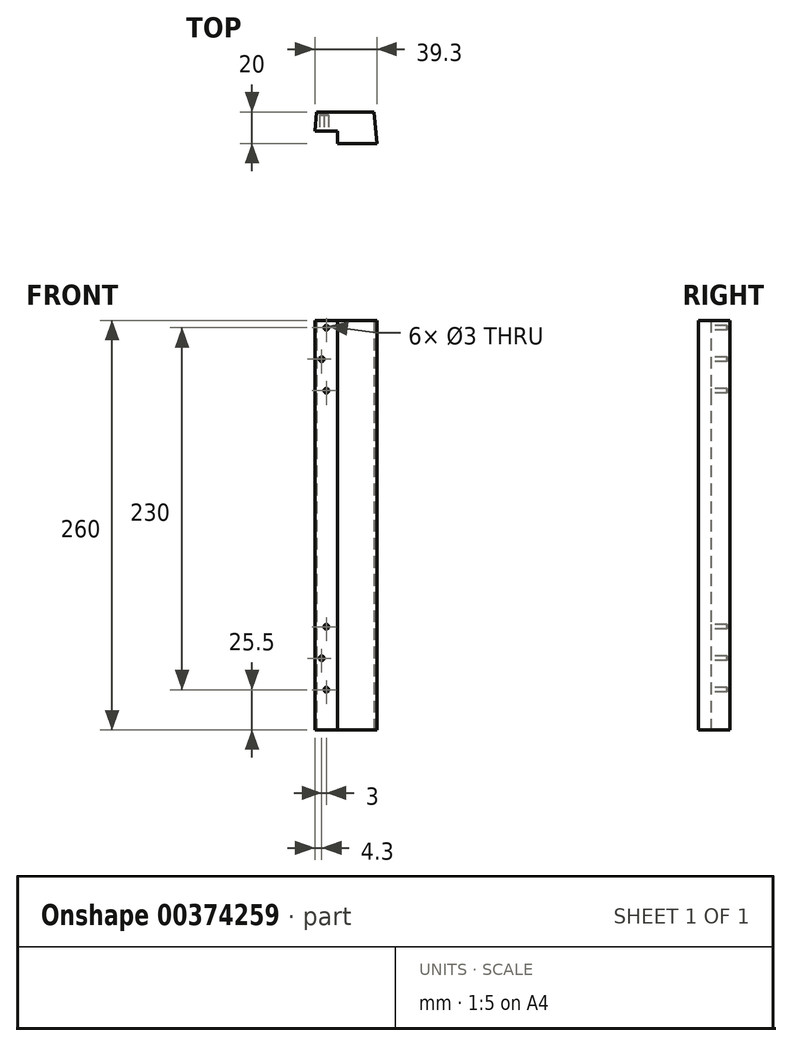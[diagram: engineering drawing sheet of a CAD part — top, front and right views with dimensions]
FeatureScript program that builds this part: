
annotation { "Feature Type Name" : "Feature", "Feature Type Description" : "" }
export const myFeature = defineFeature(function(context is Context, id is Id, definition is map)
    precondition{}
    {
        {
            var Q0;
            Q0=qCreatedBy(makeId("Top.planeOp"),FACE);
            var sketch = newSketch(context, id + "F0", { "sketchPlane" : qUnion([Q0])});
            skLineSegment(sketch, "E0", {"start": v(0.7, 8) * mm, "end": v(1.75, 20) * mm});
            skLineSegment(sketch, "E1", {"start": v(1.75, 20) * mm, "end": v(38.25, 20) * mm});
            skLineSegment(sketch, "E2", {"start": v(38.25, 20) * mm, "end": v(40, 0) * mm});
            skLineSegment(sketch, "E3", {"start": v(40, 0) * mm, "end": v(15, 0) * mm});
            skLineSegment(sketch, "E4", {"start": v(0.7, 8) * mm, "end": v(15, 8) * mm});
            skLineSegment(sketch, "E5", {"start": v(15, 8) * mm, "end": v(15, 0) * mm});
            skSolve(sketch);
        }
        {
            var Q0;
            Q0=makeQuery(id+"F0.imprint","IMPRINT",FACE,{"disambiguationData":[TD([[makeQuery(id+"F0.imprint","IMPRINT",EDGE,{"derivedFrom":sQuery(id+"F0.wireOp",EDGE,"E0")}),-1.0]])]});
            extrude(context, id + "F1", {"entities" : qUnion([Q0]), "depth" : 260 * mm});
        }
        {
            var Q0;
            Q0=makeQuery(id+"F1.opExtrude","SWEPT_FACE",FACE,{"disambiguationData":[OSD([sQuery(id+"F0.wireOp",EDGE,"E3")])]});
            var sketch = newSketch(context, id + "F2", { "sketchPlane" : qUnion([Q0])});
            skPoint(sketch, "E6", {"position": v(8, 255.5) * mm});
            skPoint(sketch, "E7", {"position": v(8, 215.5) * mm});
            skPoint(sketch, "E8", {"position": v(8, 65.5) * mm});
            skPoint(sketch, "E9", {"position": v(8, 25.5) * mm});
            skPoint(sketch, "E10", {"position": v(5, 45.5) * mm});
            skPoint(sketch, "E11", {"position": v(5, 235.5) * mm});
            skSolve(sketch);
        }
        {
            var Q0;
            Q0=sQuery(id+"F2.wireOp",VERTEX,"E6");
            var Q1;
            Q1=sQuery(id+"F2.wireOp",VERTEX,"E11");
            var Q2;
            Q2=sQuery(id+"F2.wireOp",VERTEX,"E7");
            var Q3;
            Q3=sQuery(id+"F2.wireOp",VERTEX,"E8");
            var Q4;
            Q4=sQuery(id+"F2.wireOp",VERTEX,"E10");
            var Q5;
            Q5=sQuery(id+"F2.wireOp",VERTEX,"E9");
            var Q6;
            Q6=makeQuery(id+"F1.opExtrude","SWEPT_BODY",BODY,{"disambiguationData":[OSD([sQuery(id+"F0.wireOp",EDGE,"E0"),sQuery(id+"F0.wireOp",EDGE,"E1"),sQuery(id+"F0.wireOp",EDGE,"E2"),sQuery(id+"F0.wireOp",EDGE,"E3")])]});
            hole(context, id + "F3", {"style" : HoleStyle.SIMPLE, "endStyle" : HoleEndStyle.BLIND, "holeDiameter" : 3 * mm, "holeDepth" : 10 * mm, "isTappedThrough" : true, "tappedDepth" : 12 * mm, "tapClearance" : 3, "locations" : qUnion([Q0, Q1, Q2, Q3, Q4, Q5]), "scope" : qUnion([Q6])});
        }
    });
